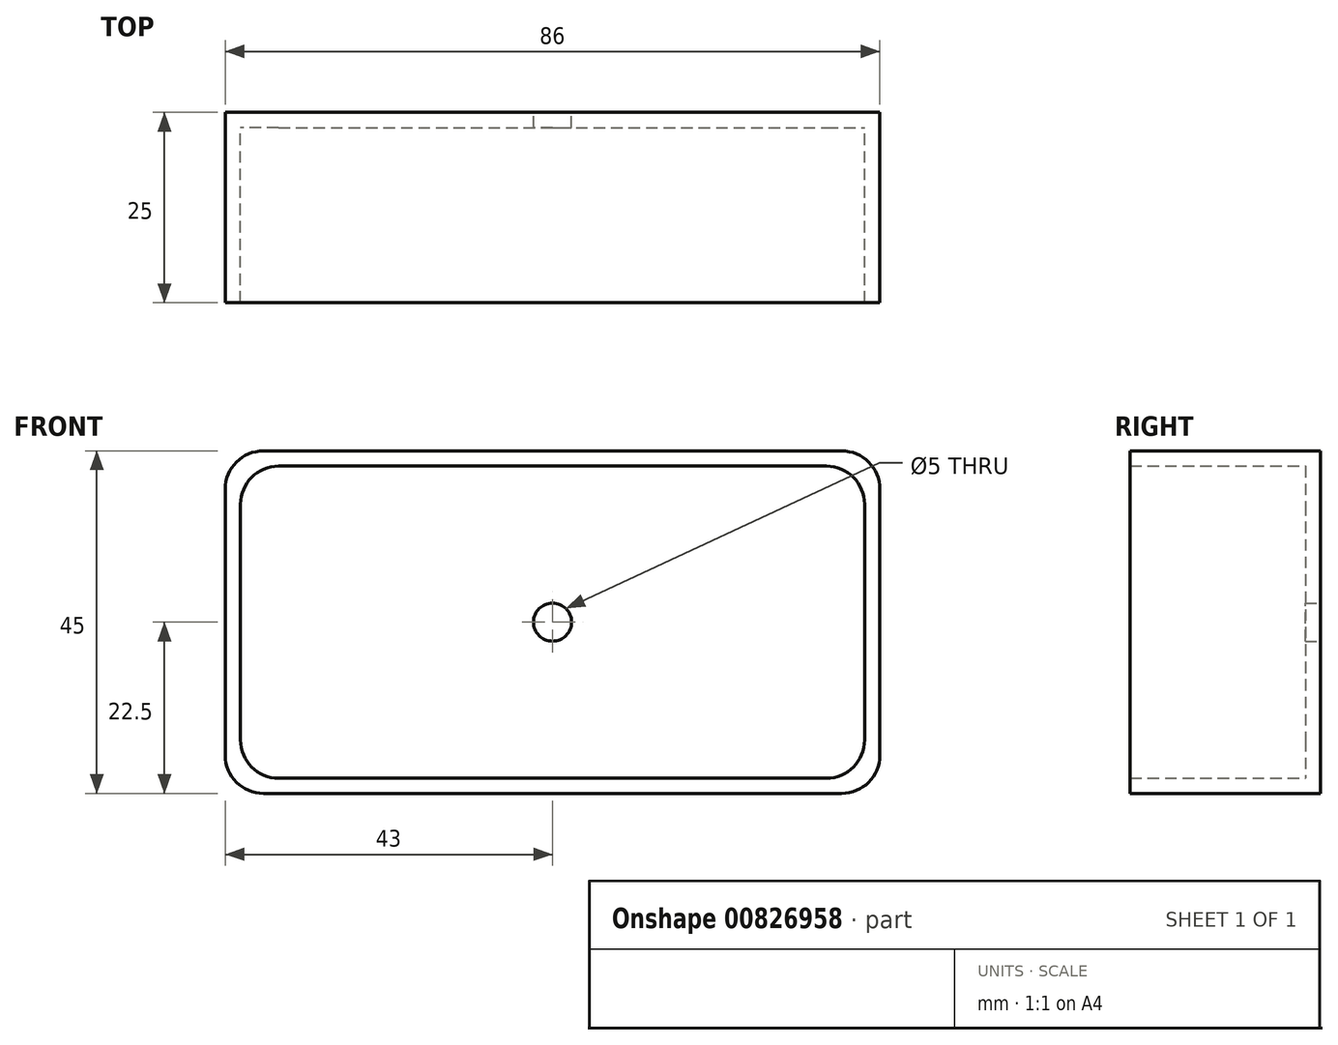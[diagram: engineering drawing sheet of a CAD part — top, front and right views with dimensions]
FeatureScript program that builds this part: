
annotation { "Feature Type Name" : "Feature", "Feature Type Description" : "" }
export const myFeature = defineFeature(function(context is Context, id is Id, definition is map)
    precondition{}
    {
        {
            var Q0;
            Q0=qCreatedBy(makeId("Front.planeOp"),FACE);
            var sketch = newSketch(context, id + "F0", { "sketchPlane" : qUnion([Q0])});
            skLineSegment(sketch, "E0.bottom", {"start": v(-41, 20.5) * mm, "end": v(41, 20.5) * mm});
            skLineSegment(sketch, "E0.top", {"start": v(-41, -20.5) * mm, "end": v(41, -20.5) * mm});
            skLineSegment(sketch, "E0.left", {"start": v(-41, 20.5) * mm, "end": v(-41, -20.5) * mm});
            skLineSegment(sketch, "E0.right", {"start": v(41, 20.5) * mm, "end": v(41, -20.5) * mm});
            skPoint(sketch, "E0.middle", {"position": v(0, 0) * mm});
            skLineSegment(sketch, "E1.0", {"start": v(-43, 22.5) * mm, "end": v(-43, -22.5) * mm});
            skLineSegment(sketch, "E1.1", {"start": v(-43, 22.5) * mm, "end": v(43, 22.5) * mm});
            skLineSegment(sketch, "E1.2", {"start": v(43, 22.5) * mm, "end": v(43, -22.5) * mm});
            skLineSegment(sketch, "E1.3", {"start": v(-43, -22.5) * mm, "end": v(43, -22.5) * mm});
            skSolve(sketch);
        }
        {
            var Q0;
            Q0=makeQuery(id+"F0.imprint","IMPRINT",FACE,{"disambiguationData":[TD([[makeQuery(id+"F0.imprint","IMPRINT",EDGE,{"derivedFrom":sQuery(id+"F0.wireOp",EDGE,"E0.bottom")}),-1.0]])]});
            extrude(context, id + "F1", {"entities" : qUnion([Q0]), "depth" : 2 * mm, "offsetDistance" : 25 * mm});
        }
        {
            var Q0;
            Q0=makeQuery(id+"F0.imprint","IMPRINT",FACE,{"disambiguationData":[TD([[makeQuery(id+"F0.imprint","IMPRINT",EDGE,{"derivedFrom":sQuery(id+"F0.wireOp",EDGE,"E0.bottom")}),1.0]])]});
            extrude(context, id + "F2", {"entities" : qUnion([Q0]), "operationType" : NewBodyOperationType.ADD, "depth" : 25 * mm, "offsetDistance" : 25 * mm});
        }
        {
            var Q0;
            Q0=makeQuery(id+"F2.opExtrude","SWEPT_EDGE",EDGE,{"disambiguationData":[OSD([sQuery(id+"F0.wireOp",EDGE,"E1.1"),sQuery(id+"F0.wireOp",EDGE,"E1.2")])]});
            var Q1;
            Q1=makeQuery(id+"F2.opExtrude","SWEPT_EDGE",EDGE,{"disambiguationData":[OSD([sQuery(id+"F0.wireOp",EDGE,"E1.0"),sQuery(id+"F0.wireOp",EDGE,"E1.3")])]});
            var Q2;
            Q2=makeQuery(id+"F2.opExtrude","SWEPT_EDGE",EDGE,{"disambiguationData":[OSD([sQuery(id+"F0.wireOp",EDGE,"E1.0"),sQuery(id+"F0.wireOp",EDGE,"E1.1")])]});
            var Q3;
            Q3=makeQuery(id+"F2.opExtrude","SWEPT_EDGE",EDGE,{"disambiguationData":[OSD([sQuery(id+"F0.wireOp",EDGE,"E1.2"),sQuery(id+"F0.wireOp",EDGE,"E1.3")])]});
            var Q4;
            Q4=makeQuery(id+"F2.opExtrude","SWEPT_EDGE",EDGE,{"disambiguationData":[OSD([sQuery(id+"F0.wireOp",EDGE,"E0.top"),sQuery(id+"F0.wireOp",EDGE,"E0.right")])]});
            var Q5;
            Q5=makeQuery(id+"F2.opExtrude","SWEPT_EDGE",EDGE,{"disambiguationData":[OSD([sQuery(id+"F0.wireOp",EDGE,"E0.top"),sQuery(id+"F0.wireOp",EDGE,"E0.left")])]});
            var Q6;
            Q6=makeQuery(id+"F2.opExtrude","SWEPT_EDGE",EDGE,{"disambiguationData":[OSD([sQuery(id+"F0.wireOp",EDGE,"E0.bottom"),sQuery(id+"F0.wireOp",EDGE,"E0.right")])]});
            var Q7;
            Q7=makeQuery(id+"F2.opExtrude","SWEPT_EDGE",EDGE,{"disambiguationData":[OSD([sQuery(id+"F0.wireOp",EDGE,"E0.bottom"),sQuery(id+"F0.wireOp",EDGE,"E0.left")])]});
            fillet(context, id + "F3", {"entities" : qUnion([Q0, Q1, Q2, Q3, Q4, Q5, Q6, Q7]), "radius" : 5 * mm, "tangentPropagation" : true, "allowEdgeOverflow" : false});
        }
        {
            var Q0;
            Q0=sQuery(id+"F0.wireOp",VERTEX,"E0.middle");
            var Q1;
            Q1=makeQuery(id+"F1.opExtrude","SWEPT_BODY",BODY,{"disambiguationData":[OSD([sQuery(id+"F0.wireOp",EDGE,"E0.bottom"),sQuery(id+"F0.wireOp",EDGE,"E0.top"),sQuery(id+"F0.wireOp",EDGE,"E0.left"),sQuery(id+"F0.wireOp",EDGE,"E0.right")])]});
            hole(context, id + "F4", {"style" : HoleStyle.SIMPLE, "endStyle" : HoleEndStyle.THROUGH, "oppositeDirection" : true, "holeDiameter" : 5 * mm, "majorDiameter" : 5 * mm, "isTappedThrough" : true, "tappedDepth" : 12 * mm, "tapClearance" : 3, "locations" : qUnion([Q0]), "scope" : qUnion([Q1])});
        }
    });
